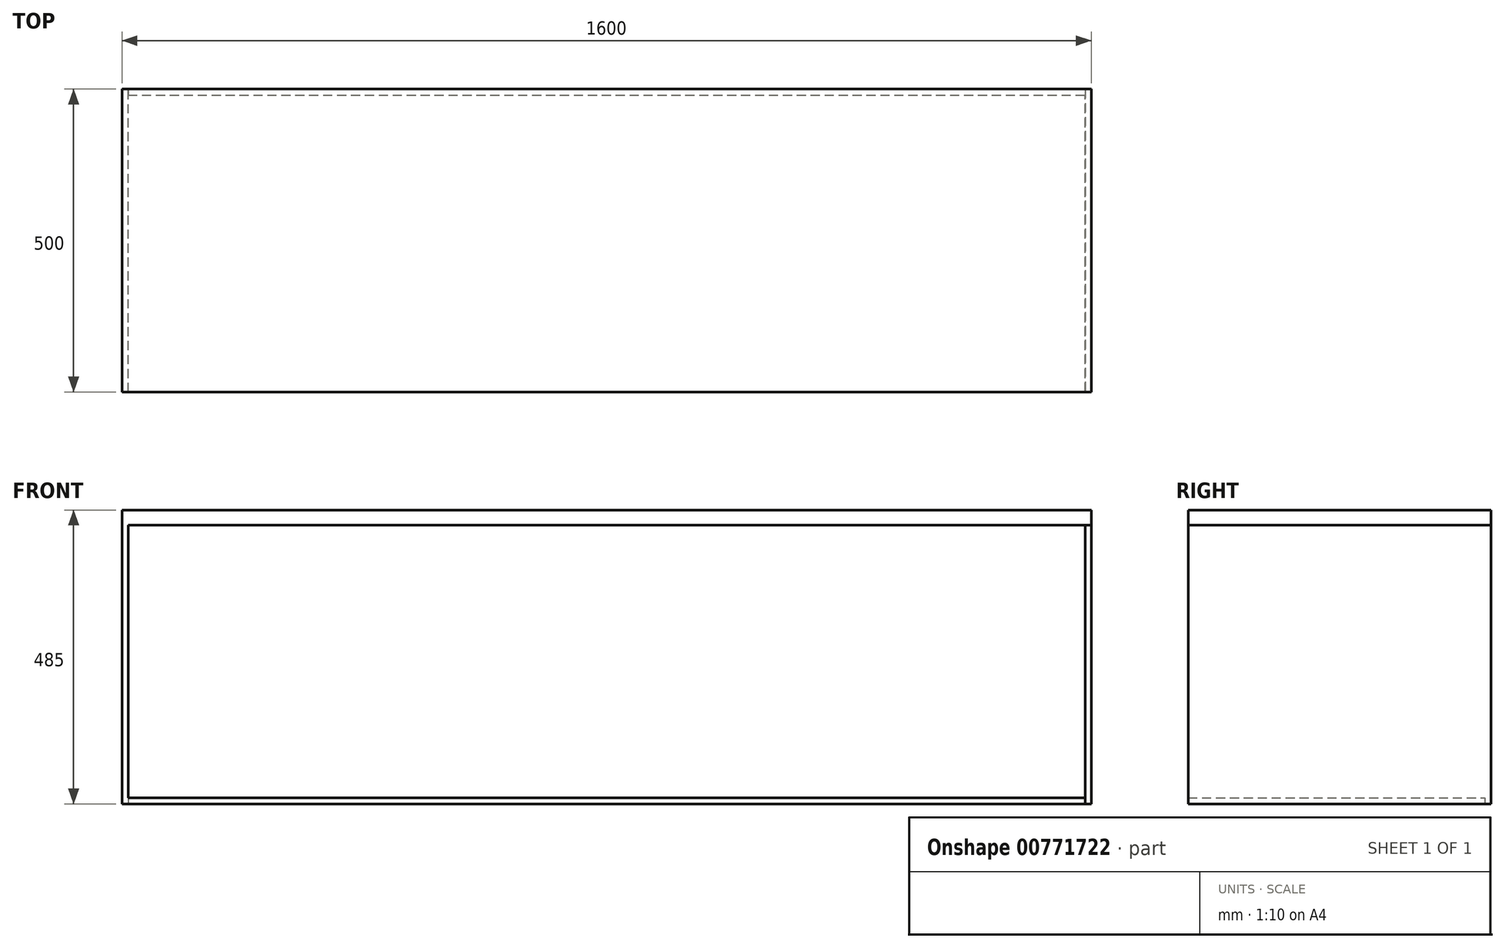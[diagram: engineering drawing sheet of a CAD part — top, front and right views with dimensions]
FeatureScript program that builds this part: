
annotation { "Feature Type Name" : "Feature", "Feature Type Description" : "" }
export const myFeature = defineFeature(function(context is Context, id is Id, definition is map)
    precondition{}
    {
        {
            var Q0;
            Q0=qCreatedBy(makeId("Top.planeOp"),FACE);
            var sketch = newSketch(context, id + "F0", { "sketchPlane" : qUnion([Q0])});
            skLineSegment(sketch, "E0.bottom", {"start": v(0, 0) * mm, "end": v(1600, 0) * mm});
            skLineSegment(sketch, "E0.top", {"start": v(0, 500) * mm, "end": v(1600, 500) * mm});
            skLineSegment(sketch, "E0.left", {"start": v(0, 0) * mm, "end": v(0, 500) * mm});
            skLineSegment(sketch, "E0.right", {"start": v(1600, 0) * mm, "end": v(1600, 500) * mm});
            skSolve(sketch);
        }
        {
            var Q0;
            Q0=makeQuery(id+"F0.imprint","IMPRINT",FACE,{"disambiguationData":[TD([[makeQuery(id+"F0.imprint","IMPRINT",EDGE,{"derivedFrom":sQuery(id+"F0.wireOp",EDGE,"E0.bottom")}),1.0]])]});
            extrude(context, id + "F1", {"entities" : qUnion([Q0]), "depth" : 25 * mm, "offsetDistance" : 25 * mm});
        }
        {
            var Q0;
            Q0=makeQuery(id+"F0.imprint","IMPRINT",FACE,{"disambiguationData":[TD([[makeQuery(id+"F0.imprint","IMPRINT",EDGE,{"derivedFrom":sQuery(id+"F0.wireOp",EDGE,"E0.bottom")}),1.0]])]});
            cPlane(context, id + "F2", {"entities" : qUnion([Q0]), "cplaneType" : CPlaneType.OFFSET, "offset" : 460 * mm, "oppositeDirection" : true, "width" : 150 * mm, "height" : 150 * mm});
        }
        {
            var Q0;
            Q0=qCreatedBy(id+"F2.planeOp",FACE);
            var sketch = newSketch(context, id + "F3", { "sketchPlane" : qUnion([Q0])});
            skLineSegment(sketch, "E1.bottom", {"start": v(10, 0) * mm, "end": v(1590, 0) * mm});
            skLineSegment(sketch, "E1.top", {"start": v(10, 490) * mm, "end": v(1590, 490) * mm});
            skLineSegment(sketch, "E1.left", {"start": v(10, 0) * mm, "end": v(10, 490) * mm});
            skLineSegment(sketch, "E1.right", {"start": v(1590, 0) * mm, "end": v(1590, 490) * mm});
            skSolve(sketch);
        }
        {
            var Q0;
            Q0=makeQuery(id+"F3.imprint","IMPRINT",FACE,{"disambiguationData":[TD([[makeQuery(id+"F3.imprint","IMPRINT",EDGE,{"derivedFrom":sQuery(id+"F3.wireOp",EDGE,"E1.bottom")}),1.0]])]});
            extrude(context, id + "F4", {"entities" : qUnion([Q0]), "depth" : 10 * mm, "offsetDistance" : 25 * mm});
        }
        {
            var Q0;
            Q0=makeQuery(id+"F0.imprint","IMPRINT",FACE,{"disambiguationData":[TD([[makeQuery(id+"F0.imprint","IMPRINT",EDGE,{"derivedFrom":sQuery(id+"F0.wireOp",EDGE,"E0.bottom")}),1.0]])]});
            var sketch = newSketch(context, id + "F5", { "sketchPlane" : qUnion([Q0])});
            skLineSegment(sketch, "E2.bottom", {"start": v(0, 0) * mm, "end": v(10, 0) * mm});
            skLineSegment(sketch, "E2.top", {"start": v(0, 500) * mm, "end": v(10, 500) * mm});
            skLineSegment(sketch, "E2.left", {"start": v(0, 0) * mm, "end": v(0, 500) * mm});
            skLineSegment(sketch, "E2.right", {"start": v(10, 0) * mm, "end": v(10, 500) * mm});
            skSolve(sketch);
        }
        {
            var Q0;
            Q0 = qSketchRegion(id + "F5", true);
            var Q1;
            Q1=makeQuery(id+"F4.opExtrude","CAP_FACE",FACE,{"disambiguationData":[OSD([sQuery(id+"F3.wireOp",EDGE,"E1.bottom"),sQuery(id+"F3.wireOp",EDGE,"E1.top"),sQuery(id+"F3.wireOp",EDGE,"E1.left"),sQuery(id+"F3.wireOp",EDGE,"E1.right")])],"isStart":true});
            extrude(context, id + "F6", {"entities" : qUnion([Q0]), "operationType" : NewBodyOperationType.ADD, "endBound" : BoundingType.UP_TO_SURFACE, "oppositeDirection" : true, "depth" : 25 * mm, "endBoundEntityFace" : qUnion([Q1]), "offsetDistance" : 25 * mm});
        }
        {
            var Q0;
            Q0=makeQuery(id+"F0.imprint","IMPRINT",FACE,{"disambiguationData":[TD([[makeQuery(id+"F0.imprint","IMPRINT",EDGE,{"derivedFrom":sQuery(id+"F0.wireOp",EDGE,"E0.bottom")}),1.0]])]});
            var sketch = newSketch(context, id + "F7", { "sketchPlane" : qUnion([Q0])});
            skLineSegment(sketch, "E3.bottom", {"start": v(1600, 0) * mm, "end": v(1590, 0) * mm});
            skLineSegment(sketch, "E3.top", {"start": v(1600, 500) * mm, "end": v(1590, 500) * mm});
            skLineSegment(sketch, "E3.left", {"start": v(1600, 0) * mm, "end": v(1600, 500) * mm});
            skLineSegment(sketch, "E3.right", {"start": v(1590, 0) * mm, "end": v(1590, 500) * mm});
            skSolve(sketch);
        }
        {
            var Q0;
            Q0=makeQuery(id+"F7.imprint","IMPRINT",FACE,{"disambiguationData":[TD([[makeQuery(id+"F7.imprint","IMPRINT",EDGE,{"derivedFrom":sQuery(id+"F7.wireOp",EDGE,"E3.bottom")}),1.0]])]});
            var Q1;
            Q1=makeQuery(id+"F4.opExtrude","CAP_FACE",FACE,{"disambiguationData":[OSD([sQuery(id+"F3.wireOp",EDGE,"E1.bottom"),sQuery(id+"F3.wireOp",EDGE,"E1.top"),sQuery(id+"F3.wireOp",EDGE,"E1.left"),sQuery(id+"F3.wireOp",EDGE,"E1.right")])],"isStart":true});
            extrude(context, id + "F8", {"entities" : qUnion([Q0]), "endBound" : BoundingType.UP_TO_SURFACE, "oppositeDirection" : true, "depth" : 25 * mm, "endBoundEntityFace" : qUnion([Q1]), "offsetDistance" : 25 * mm});
        }
    });
